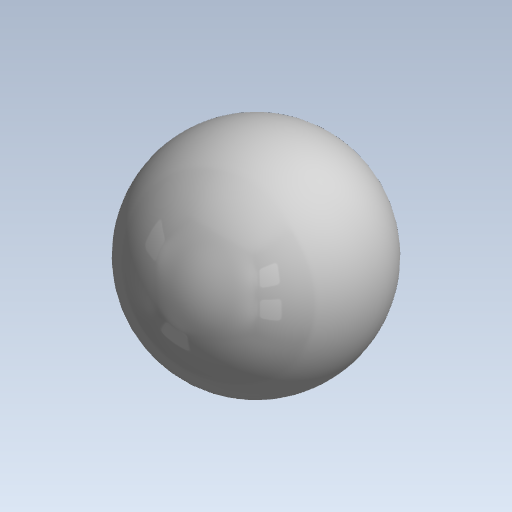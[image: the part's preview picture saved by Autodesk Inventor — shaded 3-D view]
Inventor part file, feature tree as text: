
AUTODESK INVENTOR PART (.ipt)
format: ipt  version: 2020 (Build 240168000, 168)  size: 111,104 bytes
history: native  units: mm (DEFAULTED — no unit token found)
features: revolve x1
ambient origin geometry x8: Origin, YZ Plane, XZ Plane, XY Plane, X Axis, Y Axis, Z Axis, Center Point
bodies: Solid1 (feature_tree)
feature tree (1):
  revolve  "Revolve1"  [1 undecoded]
note: 1 required parameter value undecoded (feature->parameter linkage not recoverable at this tier; creation-order binding heuristic only, values carry confidence <= 0.55)
